# Revit family: Drain_Shutoffs-Boiler-WATTS-BD_Series
name_source: partatom
category: Pipe Accessories
units: mm (PartAtom-declared; Revit-internal decimal feet)

## family parameters
Always vertical = Yes
Cut with Voids When Loaded = No
OmniClass Number = 23.65.55.14.17
OmniClass Title = Adjusting/Controlling Valves for Liquid Services
Part Type = Valve - Breaks Into
Round Connector Dimension = Use Diameter
Shared = Yes
Work Plane-Based = No

## types (7) — shared parameters
Assembly Code = D2090600
Connection Outlet Description = 3/4" Outlet Connection
Country = United States
Description = Series BD Brass Boiler Drain Shutoffs for Water Service Sizes: 1⁄2" x 3 ⁄4" – 3 ⁄4" x 3 ⁄4"
Hose Connection = 3/8"
Manufacturer = WATTS
Manufacturer Product Line = Water Safety & Flow Control
Materials = Metal-WATTS-Brass
Max. Working Pressure = 200psi (14 bar) WOG, non-shock
Maximum Temperature = 180°F (82°C)
Product Documentation Link = https://www.watts.com
Product Page URL = https://www.watts.com
Region = North America
Revised Date = 12/02/2024
URL = http://www.watts.com

## per-type parameters (varying)
| type | Angle-Straight | Center To Outlet Connection A | Connection Inlet Description | Connection Radius | Connection Size | Connection Type | Handle Width K | Height | Weight |
| BD-1C 1/2" | 30.00° | 1 11/32" | 1/2" Inlet Connection | 1/4" | 1/2" | Male IP or Solder inlet, angle | 1 21/32" | 3 1/2" | 0.5lbs. (0.24kg.) |
| BD2 3/4" | 30.00° | 1 1/2" | 3/4" Inlet Connection | 3/8" | 3/4" | Male IP inlet, angle | 2 1/8" | 3 9/16" | 0.5lbs. (0.24kg.) |
| BD-2C 3/4" | 30.00° | 1 11/32" | 3/4" Inlet Connection | 3/8" | 3/4" | Male IP inlet, angle | 2 3/32" | 3 1/2" | 0.4lbs. (0.20kg.) |
| BD3F 1/2" | 30.00° | 1 1/2" | 1/2" Inlet Connection | 1/4" | 1/2" | Female IP inlet, angle | 2 1/8" | 3 1/4" | 0.5lbs. (0.24kg.) |
| BD4F 3/4" | 30.00° | 1 1/2" | 3/4" Inlet Connection | 3/8" | 3/4" | Female IP, angle | 2 1/8" | 3 1/4" | 0.5lbs. (0.24kg.) |
| BD5 1/2" | 0.50° | 1 1/8" | 1/2" Inlet Connection | 1/4" | 1/2" | Male IP or Solder, straight | 2 1/8" | 2 15/16" | 0.4lbs. (0.20kg.) |
| BD6 3/4" | 0.50° | 1 1/8" | 3/4" Inlet Connection | 3/8" | 3/4" | Male IP or Solder, straight | 2 1/8" | 3 1/8" | 0.4lbs. (0.20kg.) |

note: column(s) folded — value = type name in every type: Model

## geometry (parser evidence)
native form markers: Sweep x2
no freeform markers — native parametric forms only
